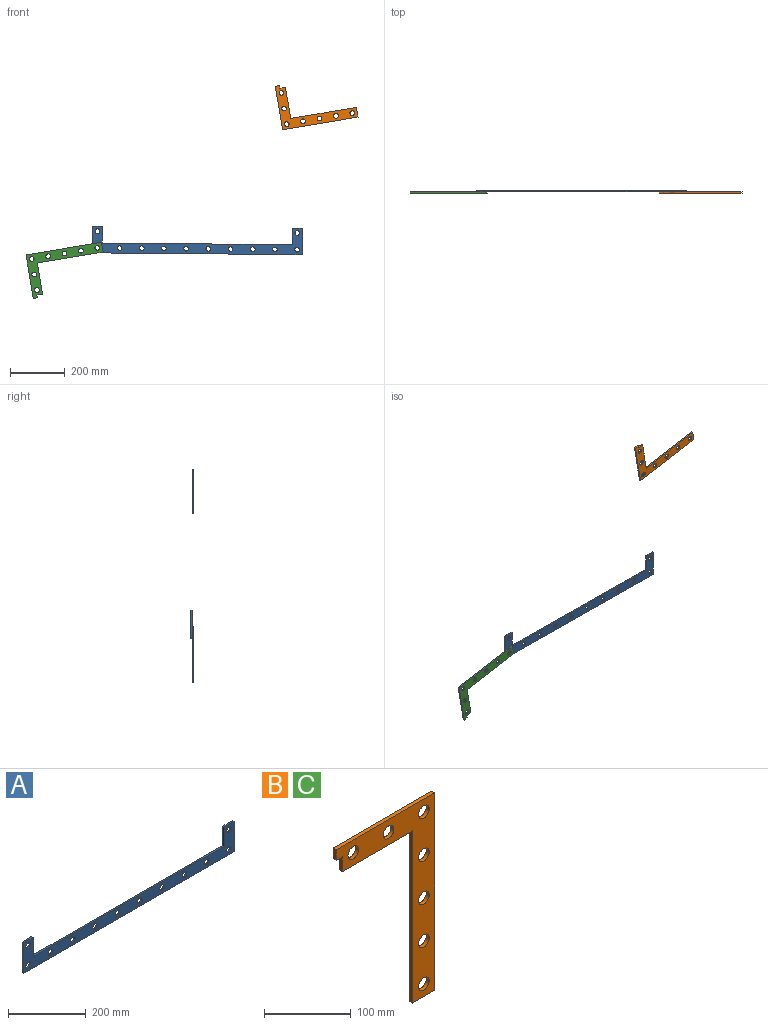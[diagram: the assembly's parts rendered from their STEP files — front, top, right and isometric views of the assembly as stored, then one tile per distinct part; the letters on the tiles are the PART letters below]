
ASSEMBLY  parts=3 mates=3
PART A: 22 faces, bbox 765x5x96.8 mm
  f0: plane 60.75x5mm, normal (1,0,0), area 303.7mm2, adj f1,f7,f8,f9
  f1: plane 36x5mm, normal (0,0,1), area 180mm2, adj f0,f2,f8,f9
  f2: plane 96.75x5mm, normal (-1,0,0), area 483.8mm2, adj f1,f3,f8,f9
  f3: plane 765x5mm, normal (0,0,-1), area 3825mm2, adj f2,f4,f8,f9
  f4: plane 96.75x5mm, normal (1,0,0), area 483.8mm2, adj f3,f5,f8,f9
  f5: plane 36x5mm, normal (0,0,1), area 180mm2, adj f4,f6,f8,f9
  f6: plane 60.75x5mm, normal (-1,0,0), area 303.7mm2, adj f5,f7,f8,f9
  f7: plane 693x5mm, normal (0,0,1), area 3465mm2, adj f0,f6,f8,f9
  f8: plane 765x96.75mm, normal (0,-1,0), area 29027.7mm2, adj f0,f1,f2,f3,f4,f5,f6,f7
  f9: plane 765x96.75mm, normal (0,1,0), area 29027.7mm2, adj f0,f1,f2,f3,f4,f5,f6,f7
  f10: cylinder r=8.75mm len=17.5mm, axis (0,1,0), area 274.9mm2, adj f8,f9
  f11: cylinder r=8.75mm len=17.5mm, axis (0,1,0), area 274.9mm2, adj f8,f9
  f12: cylinder r=8.75mm len=17.5mm, axis (0,1,0), area 274.9mm2, adj f8,f9
  f13: cylinder r=8.75mm len=17.5mm, axis (0,1,0), area 274.9mm2, adj f8,f9
  f14: cylinder r=8.75mm len=17.5mm, axis (0,1,0), area 274.9mm2, adj f8,f9
  f15: cylinder r=8.75mm len=17.5mm, axis (0,1,0), area 274.9mm2, adj f8,f9
  f16: cylinder r=8.75mm len=17.5mm, axis (0,1,0), area 274.9mm2, adj f8,f9
  f17: cylinder r=8.75mm len=17.5mm, axis (0,1,0), area 274.9mm2, adj f8,f9
  f18: cylinder r=8.75mm len=17.5mm, axis (0,1,0), area 274.9mm2, adj f8,f9
  f19: cylinder r=8.75mm len=17.5mm, axis (0,1,0), area 274.9mm2, adj f8,f9
  f20: cylinder r=8.75mm len=17.5mm, axis (0,1,0), area 274.9mm2, adj f8,f9
  f21: cylinder r=8.75mm len=17.5mm, axis (0,1,0), area 274.9mm2, adj f8,f9
PART B: 17 faces, bbox 161x5x279 mm
  f0: plane 161x5mm, normal (0,0,1), area 805mm2, adj f1,f7,f8,f9
  f1: plane 15x5mm, normal (-1,0,0), area 75mm2, adj f0,f2,f8,f9
  f2: plane 10x5mm, normal (0,0,-1), area 50mm2, adj f1,f3,f8,f9
  f3: plane 21x5mm, normal (-1,0,0), area 105mm2, adj f2,f4,f8,f9
  f4: plane 115x5mm, normal (0,0,-1), area 575mm2, adj f3,f5,f8,f9
  f5: plane 243x5mm, normal (-1,0,0), area 1215mm2, adj f4,f6,f8,f9
  f6: plane 36x5mm, normal (0,0,-1), area 180mm2, adj f5,f7,f8,f9
  f7: plane 279x5mm, normal (1,0,0), area 1395mm2, adj f0,f6,f8,f9
  f8: plane 279x161mm, normal (0,-1,0), area 12650.3mm2, adj f0,f1,f2,f3,f4,f5,f6,f7
  f9: plane 279x161mm, normal (0,1,0), area 12650.3mm2, adj f0,f1,f2,f3,f4,f5,f6,f7
  f10: cylinder r=8.75mm len=17.5mm, axis (0,-1,0), area 274.9mm2, adj f8,f9
  f11: cylinder r=8.75mm len=17.5mm, axis (0,-1,0), area 274.9mm2, adj f8,f9
  f12: cylinder r=8.75mm len=17.5mm, axis (0,-1,0), area 274.9mm2, adj f8,f9
  f13: cylinder r=8.75mm len=17.5mm, axis (0,-1,0), area 274.9mm2, adj f8,f9
  f14: cylinder r=8.75mm len=17.5mm, axis (0,-1,0), area 274.9mm2, adj f8,f9
  f15: cylinder r=8.75mm len=17.5mm, axis (0,-1,0), area 274.9mm2, adj f8,f9
  f16: cylinder r=8.75mm len=17.5mm, axis (0,-1,0), area 274.9mm2, adj f8,f9
PART C: same geometry as B
PLACE A rot(axis=(0,1,0),0.5deg) t=(133.16,-36.66,-533.35)mm fixed
PLACE B rot(axis=(0.76,0,-0.65),180deg) t=(763.81,-46.66,-21.94)mm
PLACE C rot(axis=(0,-1,0),99.5deg) t=(-119.3,-41.66,-796.1)mm
MATE planar B.f14 <-> A.f8  axis (0,1,0) through (984.94,-41.66,-129.89)mm
MATE cylindrical C.f16 <-> A.f10  axis (0,-1,0) through (114.49,-44.16,-611.94)mm
MATE planar C.f9 <-> A.f8  axis (0,1,0) through (-37.73,-41.66,-660.83)mm
